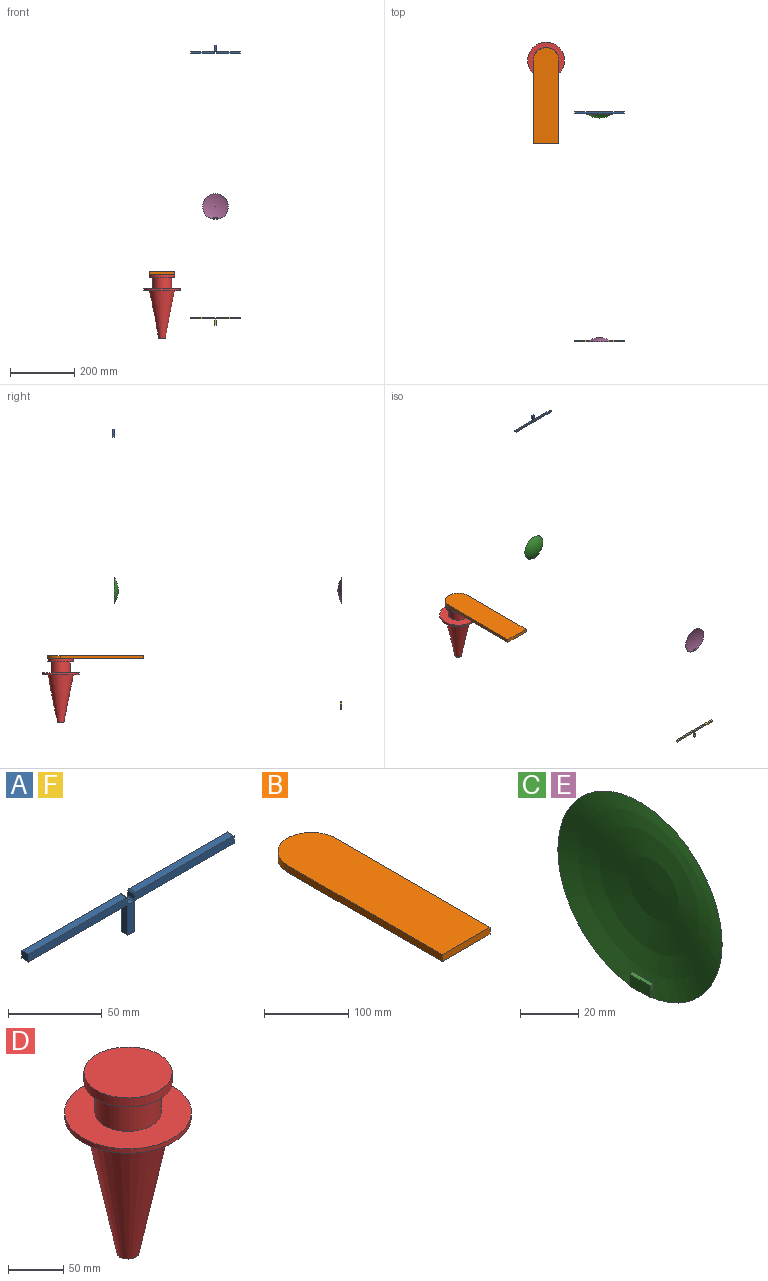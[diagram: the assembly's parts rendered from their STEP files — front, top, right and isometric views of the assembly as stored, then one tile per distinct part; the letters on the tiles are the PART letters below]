
ASSEMBLY  parts=6 mates=1
PART A: 20 faces, bbox 155x5x25 mm
  f0: cylinder r=1mm len=5mm, axis (0,1,0), area 7.9mm2, adj f1,f17,f18,f19
  f1: plane 19x5mm, normal (-1,0,0), area 95mm2, adj f0,f2,f18,f19
  f2: plane 5x5mm, normal (0,0,-1), area 25mm2, adj f1,f3,f18,f19
  f3: plane 19x5mm, normal (1,0,0), area 95mm2, adj f2,f4,f18,f19
  f4: cylinder r=1mm len=5mm, axis (0,1,0), area 7.9mm2, adj f3,f5,f18,f19
  f5: plane 74x5mm, normal (0,0,-1), area 370mm2, adj f4,f6,f18,f19
  f6: plane 5x5mm, normal (1,0,0), area 25mm2, adj f5,f7,f18,f19
  f7: plane 74x5mm, normal (0,0,1), area 370mm2, adj f6,f8,f18,f19
  f8: cylinder r=1mm len=5mm, axis (0,1,0), area 7.9mm2, adj f7,f9,f18,f19
  f9: plane 5x3mm, normal (-1,0,0), area 15mm2, adj f8,f10,f18,f19
  f10: cylinder r=1mm len=5mm, axis (0,1,0), area 7.9mm2, adj f9,f11,f18,f19
  f11: plane 5x3mm, normal (0,0,1), area 15mm2, adj f10,f12,f18,f19
  f12: cylinder r=1mm len=5mm, axis (0,1,0), area 7.9mm2, adj f11,f13,f18,f19
  f13: plane 5x3mm, normal (1,0,0), area 15mm2, adj f12,f14,f18,f19
  f14: cylinder r=1mm len=5mm, axis (0,1,0), area 7.9mm2, adj f13,f15,f18,f19
  f15: plane 74x5mm, normal (0,0,1), area 370mm2, adj f14,f16,f18,f19
  f16: plane 5x5mm, normal (-1,0,0), area 25mm2, adj f15,f17,f18,f19
  f17: plane 74x5mm, normal (0,0,-1), area 370mm2, adj f0,f16,f18,f19
  f18: plane 155x25mm, normal (0,-1,0), area 850.4mm2, adj f0,f1,f2,f3,f4,f5,f6,f7
  f19: plane 155x25mm, normal (0,1,0), area 850.4mm2, adj f0,f1,f2,f3,f4,f5,f6,f7
PART B: 6 faces, bbox 80x300x10 mm
  f0: plane 260x10mm, normal (1,0,0), area 2600mm2, adj f1,f3,f4,f5
  f1: cylinder r=40mm len=80mm, axis (0,0,-1), area 1256.6mm2, adj f0,f2,f4,f5
  f2: plane 260x10mm, normal (-1,0,0), area 2600mm2, adj f1,f3,f4,f5
  f3: plane 80x10mm, normal (0,-1,0), area 800mm2, adj f0,f2,f4,f5
  f4: plane 300x80mm, normal (0,0,1), area 23313.3mm2, adj f0,f1,f2,f3
  f5: plane 300x80mm, normal (0,0,-1), area 23313.3mm2, adj f0,f1,f2,f3
PART C: 10 faces, bbox 12x80x80 mm
  f0: revolved ~80x80mm, area 5429mm2, adj f1,f3,f4,f6
  f1: torus R=1.89mm, axis (-1,0,0), area 5137.7mm2, adj f0,f7,f8,f9
  f2: plane 10x5mm, normal (-1,0,0), area 50mm2, adj f3,f4,f5,f7,f8,f9
  f3: plane 3.65x2.02mm, normal (0,-1,0), area 3.9mm2, adj f0,f2,f5,f6
  f4: plane 3.65x2.02mm, normal (0,1,0), area 3.9mm2, adj f0,f2,f5,f6
  f5: plane 10x2mm, normal (0,0,-1), area 20mm2, adj f2,f3,f4,f6
  f6: plane 10x3.62mm, normal (1,0,0), area 33.9mm2, adj f0,f3,f4,f5
  f7: plane 10.01x1.76mm, normal (0,0,1), area 17.2mm2, adj f1,f2,f8,f9
  f8: plane 4.73x1.68mm, normal (0,-1,0), area 3.9mm2, adj f1,f2,f7
  f9: plane 4.73x1.68mm, normal (0,1,0), area 3.9mm2, adj f1,f2,f7
PART D: 9 faces, bbox 115x115x200 mm
  f0: plane 80x80mm, normal (0,0,1), area 5026.5mm2, adj f8
  f1: plane 20x20mm, normal (0,0,-1), area 314.2mm2, adj f2
  f2: cone r=10mm half-angle=11.2deg, axis (0,0,1), area 24160.5mm2, adj f1,f3
  f3: plane 115x115mm, normal (0,0,-1), area 5360.3mm2, adj f2,f4
  f4: cylinder r=57.5mm len=115mm, axis (0,0,1), area 1806.4mm2, adj f3,f5
  f5: plane 115x115mm, normal (0,0,1), area 7559.5mm2, adj f4,f6
  f6: cylinder r=30mm len=60mm, axis (0,0,1), area 6435.8mm2, adj f5,f7
  f7: plane 80x80mm, normal (0,0,-1), area 2199.1mm2, adj f6,f8
  f8: cylinder r=40mm len=80mm, axis (0,0,1), area 2513.3mm2, adj f0,f7
PART E: same geometry as C
PART F: same geometry as A
PLACE A rot(axis=(0,1,0),180deg) t=(-97.15,360.5,1683.86)mm
PLACE B t=(-166.69,1319.11,32.27)mm
PLACE C rot(axis=(0,0,-1),90deg) t=(13.58,-24.79,415)mm
PLACE D t=(-166.69,1319.11,32.27)mm
PLACE E rot(axis=(0,0,1),90deg) t=(-13.58,23.79,415)mm
PLACE F t=(97.15,-350.5,-720.02)mm
MATE fastened B.f1 <-> D.f2  axis (0,0,-1) through (-166.69,522.32,202.02)mm
